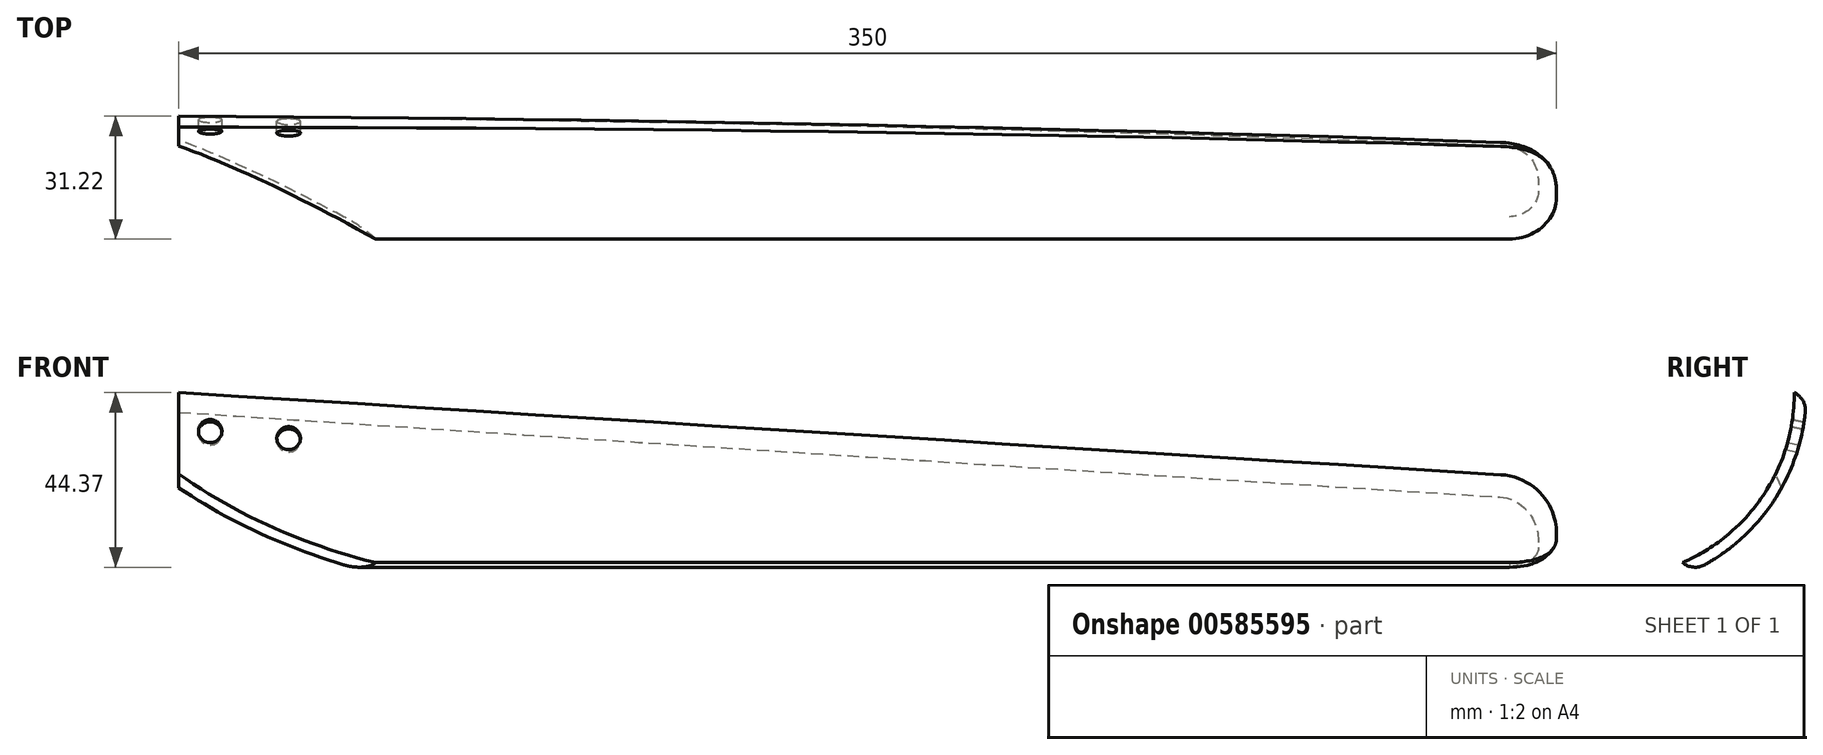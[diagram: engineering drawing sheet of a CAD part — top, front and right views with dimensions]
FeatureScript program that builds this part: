
annotation { "Feature Type Name" : "Feature", "Feature Type Description" : "" }
export const myFeature = defineFeature(function(context is Context, id is Id, definition is map)
    precondition{}
    {
        {
            assignVariable(context, id + "F0", {"name" : "longueur", "anyValue" : 350});
        }
        {
            var Q0;
            Q0=qCreatedBy(makeId("Right.planeOp"),FACE);
            var sketch = newSketch(context, id + "F1", { "sketchPlane" : qUnion([Q0])});
            skCircle(sketch, "E0", {"center": v(0, 0) * mm, "radius": 50 * mm});
            skCircle(sketch, "E1.0", {"center": v(0, 0) * mm, "radius": 47 * mm});
            skLineSegment(sketch, "E2", {"start": v(50, 0) * mm, "end": v(19.75, -45.93) * mm, "construction": true});
            skLineSegment(sketch, "E3", {"start": v(50, 0) * mm, "end": v(47, 0) * mm});
            skLineSegment(sketch, "E4", {"start": v(19.75, -45.93) * mm, "end": v(18.57, -43.18) * mm});
            skLineSegment(sketch, "E5", {"start": v(50, 0) * mm, "end": v(43.75, -24.2) * mm, "construction": true});
            skLineSegment(sketch, "E6", {"start": v(0, 0) * mm, "end": v(50, 0) * mm, "construction": true});
            skLineSegment(sketch, "E7.1.0", {"start": v(0, 0) * mm, "end": v(49.06, -9.65) * mm, "construction": true});
            skLineSegment(sketch, "E7.2.0", {"start": v(0, 0) * mm, "end": v(46.28, -18.93) * mm, "construction": true});
            skLineSegment(sketch, "E7.anchor2", {"start": v(0, 0) * mm, "end": v(19.75, -45.93) * mm, "construction": true});
            skLineSegment(sketch, "E8.2.3.0", {"start": v(0, 0) * mm, "end": v(41.76, -27.5) * mm, "construction": true});
            skLineSegment(sketch, "E8.2.4.0", {"start": v(0, 0) * mm, "end": v(35.67, -35.04) * mm, "construction": true});
            skLineSegment(sketch, "E9.2.5.0", {"start": v(0, 0) * mm, "end": v(28.24, -41.26) * mm, "construction": true});
            skSolve(sketch);
        }
        {
            var Q0;
            {var subQ0=sQuery(id+"F1.wireOp",EDGE,"E3");Q0=makeQuery(id+"F1.imprint","IMPRINT",FACE,{"disambiguationData":[TD([[makeQuery(id+"F1.imprint","IMPRINT",EDGE,{"derivedFrom":subQ0}),1.0]])]});}
            extrude(context, id + "F2", {"entities" : qUnion([Q0]), "depth" : (getVariable(context, 'longueur')) * mm, "offsetDistance" : 25 * mm});
        }
        {
            var Q0;
            Q0=makeQuery(id+"F2.opExtrude","CAP_FACE",FACE,{"disambiguationData":[OSD([sQuery(id+"F1.wireOp",EDGE,"E0"),sQuery(id+"F1.wireOp",EDGE,"E1.0"),sQuery(id+"F1.wireOp",EDGE,"E3"),sQuery(id+"F1.wireOp",EDGE,"E4")])],"isStart":false});
            var sketch = newSketch(context, id + "F3", { "sketchPlane" : qUnion([Q0])});
            skLineSegment(sketch, "E10", {"start": v(19.75, -45.93) * mm, "end": v(45.03, -21.73) * mm});
            skSolve(sketch);
        }
        {
            var Q0;
            Q0=makeQuery(id+"F2.opExtrude","CAP_VERTEX",VERTEX,{"disambiguationData":[OSD([sQuery(id+"F1.wireOp",EDGE,"E1.0"),sQuery(id+"F1.wireOp",EDGE,"E3")])],"isStart":true});
            var Q1;
            Q1=makeQuery(id+"F2.opExtrude","CAP_VERTEX",VERTEX,{"disambiguationData":[OSD([sQuery(id+"F1.wireOp",EDGE,"E0"),sQuery(id+"F1.wireOp",EDGE,"E3")])],"isStart":true});
            var Q2;
            Q2=sQuery(id+"F3.wireOp",VERTEX,"E10.end");
            cPlane(context, id + "F4", {"entities" : qUnion([Q0, Q1, Q2]), "cplaneType" : CPlaneType.THREE_POINT, "offset" : 25 * mm, "width" : 150 * mm, "height" : 150 * mm});
        }
        {
            var Q0;
            Q0=qCreatedBy(id+"F4.planeOp",FACE);
            var sketch = newSketch(context, id + "F5", { "sketchPlane" : qUnion([Q0])});
            skLineSegment(sketch, "E11.0", {"start": v(0, 50) * mm, "end": v(0, 47) * mm});
            skLineSegment(sketch, "E12", {"start": v(0, 50) * mm, "end": v(356.03, 68.4) * mm});
            skLineSegment(sketch, "E13", {"start": v(356.03, 68.4) * mm, "end": v(352, 18.56) * mm});
            skLineSegment(sketch, "E14", {"start": v(352, 18.57) * mm, "end": v(0, 47) * mm});
            skSolve(sketch);
        }
        {
            var Q0;
            Q0 = qSketchRegion(id + "F5", true);
            extrude(context, id + "F6", {"entities" : qUnion([Q0]), "operationType" : NewBodyOperationType.REMOVE, "endBound" : BoundingType.THROUGH_ALL, "depth" : 25 * mm, "offsetDistance" : 25 * mm});
        }
        {
            var Q0;
            Q0=makeQuery(id+"F2.opExtrude","SWEPT_FACE",FACE,{"disambiguationData":[OSD([sQuery(id+"F1.wireOp",EDGE,"E4")])]});
            var sketch = newSketch(context, id + "F7", { "sketchPlane" : qUnion([Q0])});
            skLineSegment(sketch, "E15", {"start": v(0, -50) * mm, "end": v(50, -50) * mm});
            skLineSegment(sketch, "E16", {"start": v(50, -50) * mm, "end": v(50, -47) * mm});
            skSolve(sketch);
        }
        {
            var Q0;
            Q0=sQuery(id+"F7.wireOp",VERTEX,"E15.end");
            var Q1;
            Q1=sQuery(id+"F7.wireOp",VERTEX,"E16.end");
            var Q2;
            Q2=sQuery(id+"F1.wireOp",VERTEX,"E5.end");
            cPlane(context, id + "F8", {"entities" : qUnion([Q0, Q1, Q2]), "cplaneType" : CPlaneType.THREE_POINT, "offset" : 25 * mm, "width" : 150 * mm, "height" : 150 * mm});
        }
        {
            var Q0;
            Q0=qCreatedBy(id+"F8.planeOp",FACE);
            var sketch = newSketch(context, id + "F9", { "sketchPlane" : qUnion([Q0])});
            skLineSegment(sketch, "E17.bottom", {"start": v(26.95, -18.07) * mm, "end": v(-72.05, -18.07) * mm});
            skLineSegment(sketch, "E17.top", {"start": v(26.95, -70.26) * mm, "end": v(-72.05, -70.26) * mm});
            skLineSegment(sketch, "E17.left", {"start": v(26.95, -18.07) * mm, "end": v(26.95, -70.26) * mm});
            skLineSegment(sketch, "E17.right", {"start": v(-72.05, -18.07) * mm, "end": v(-72.05, -70.26) * mm});
            skSolve(sketch);
        }
        {
            var Q0;
            Q0 = qSketchRegion(id + "F9", true);
            extrude(context, id + "F10", {"entities" : qUnion([Q0]), "operationType" : NewBodyOperationType.REMOVE, "endBound" : BoundingType.THROUGH_ALL, "oppositeDirection" : true, "depth" : 25 * mm, "offsetDistance" : 25 * mm});
        }
        {
            var Q0;
            Q0=makeQuery(id+"F6.boolean.opBoolean","INTERSECT",EDGE,{"derivedFrom":[makeQuery(id+"F2.opExtrude","CAP_FACE",FACE,{"disambiguationData":[OSD([sQuery(id+"F1.wireOp",EDGE,"E0"),sQuery(id+"F1.wireOp",EDGE,"E1.0"),sQuery(id+"F1.wireOp",EDGE,"E3"),sQuery(id+"F1.wireOp",EDGE,"E4")])],"isStart":false}),makeQuery(id+"F6.opExtrude","CAP_FACE",FACE,{"disambiguationData":[OSD([sQuery(id+"F5.wireOp",EDGE,"E11.0"),sQuery(id+"F5.wireOp",EDGE,"E12"),sQuery(id+"F5.wireOp",EDGE,"E13"),sQuery(id+"F5.wireOp",EDGE,"E14")])],"isStart":true})]});
            fillet(context, id + "F11", {"entities" : qUnion([Q0]), "radius" : 15 * mm, "tangentPropagation" : true, "allowEdgeOverflow" : false});
        }
        {
            var Q0;
            Q0=makeQuery(id+"F2.opExtrude","CAP_EDGE",EDGE,{"disambiguationData":[OSD([sQuery(id+"F1.wireOp",EDGE,"E4")])],"isStart":false});
            fillet(context, id + "F12", {"entities" : qUnion([Q0]), "radius" : 12 * mm, "tangentPropagation" : true, "allowEdgeOverflow" : false});
        }
        {
            var Q0;
            Q0=makeQuery(id+"F6.boolean.opBoolean","INTERSECT",EDGE,{"derivedFrom":[makeQuery(id+"F2.opExtrude","SWEPT_FACE",FACE,{"disambiguationData":[OSD([sQuery(id+"F1.wireOp",EDGE,"E0")])]}),makeQuery(id+"F6.opExtrude","CAP_FACE",FACE,{"disambiguationData":[OSD([sQuery(id+"F5.wireOp",EDGE,"E11.0"),sQuery(id+"F5.wireOp",EDGE,"E12"),sQuery(id+"F5.wireOp",EDGE,"E13"),sQuery(id+"F5.wireOp",EDGE,"E14")])],"isStart":true})]});
            fillet(context, id + "F13", {"entities" : qUnion([Q0]), "radius" : 5 * mm, "tangentPropagation" : true, "allowEdgeOverflow" : false});
        }
        {
            var Q0;
            Q0=sQuery(id+"F1.wireOp",VERTEX,"E7.1.0.end");
            var Q1;
            Q1=sQuery(id+"F1.wireOp",EDGE,"E7.1.0");
            cPlane(context, id + "F14", {"entities" : qUnion([Q0, Q1]), "cplaneType" : CPlaneType.LINE_POINT, "offset" : 25 * mm, "width" : 150 * mm, "height" : 150 * mm});
        }
        {
            var Q0;
            Q0=qCreatedBy(id+"F14.planeOp",FACE);
            var sketch = newSketch(context, id + "F15", { "sketchPlane" : qUnion([Q0])});
            skLineSegment(sketch, "E18", {"start": v(-7.97, -0.74) * mm, "end": v(-27.88, -2.58) * mm, "construction": true});
            skCircle(sketch, "E19", {"center": v(-7.97, -0.74) * mm, "radius": 3 * mm});
            skCircle(sketch, "E20", {"center": v(-27.88, -2.58) * mm, "radius": 3 * mm});
            skSolve(sketch);
        }
        {
            var Q0;
            Q0 = qSketchRegion(id + "F15", true);
            extrude(context, id + "F16", {"entities" : qUnion([Q0]), "operationType" : NewBodyOperationType.REMOVE, "endBound" : BoundingType.THROUGH_ALL, "oppositeDirection" : true, "depth" : 25 * mm, "offsetDistance" : 25 * mm});
        }
    });
